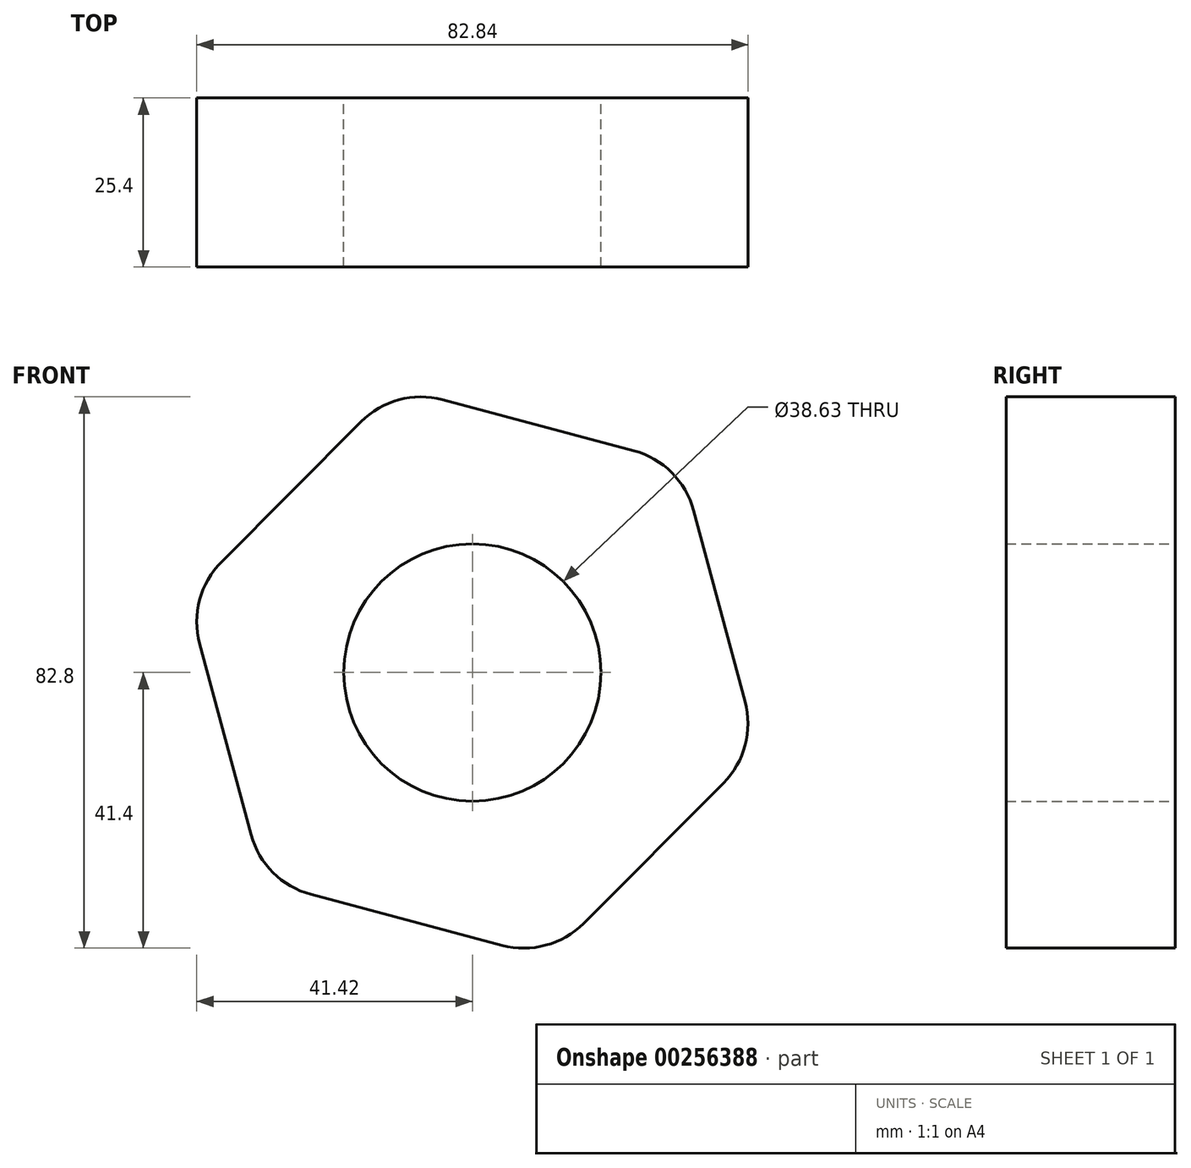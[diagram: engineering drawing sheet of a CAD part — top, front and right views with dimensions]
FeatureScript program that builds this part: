
annotation { "Feature Type Name" : "Feature", "Feature Type Description" : "" }
export const myFeature = defineFeature(function(context is Context, id is Id, definition is map)
    precondition{}
    {
        {
            var Q0;
            Q0=qCreatedBy(makeId("Front.planeOp"),FACE);
            var sketch = newSketch(context, id + "F0", { "sketchPlane" : qUnion([Q0])});
            skCircle(sketch, "E0.cCircle", {"center": v(0, 0) * mm, "radius": 44.39 * mm, "construction": true});
            skLineSegment(sketch, "E0.0", {"start": v(31.34, 31.44) * mm, "end": v(42.9, -11.42) * mm});
            skLineSegment(sketch, "E0.1", {"start": v(42.9, -11.42) * mm, "end": v(11.56, -42.86) * mm});
            skLineSegment(sketch, "E0.2", {"start": v(11.56, -42.86) * mm, "end": v(-31.34, -31.44) * mm});
            skLineSegment(sketch, "E0.3", {"start": v(-31.34, -31.44) * mm, "end": v(-42.9, 11.42) * mm});
            skLineSegment(sketch, "E0.4", {"start": v(-42.9, 11.42) * mm, "end": v(-11.56, 42.86) * mm});
            skLineSegment(sketch, "E0.5", {"start": v(-11.56, 42.86) * mm, "end": v(31.34, 31.44) * mm});
            skCircle(sketch, "E1", {"center": v(0, 0) * mm, "radius": 19.32 * mm});
            skSolve(sketch);
        }
        {
            var Q0;
            Q0 = qSketchRegion(id + "F0", true);
            extrude(context, id + "F1", {"entities" : qUnion([Q0]), "depth" : 25.4 * mm});
        }
        {
            var Q0;
            Q0=makeQuery(id+"F1.opExtrude","SWEPT_EDGE",EDGE,{"disambiguationData":[OSD([sQuery(id+"F0.wireOp",EDGE,"E0.3"),sQuery(id+"F0.wireOp",EDGE,"E0.4")])]});
            var Q1;
            Q1=makeQuery(id+"F1.opExtrude","SWEPT_EDGE",EDGE,{"disambiguationData":[OSD([sQuery(id+"F0.wireOp",EDGE,"E0.2"),sQuery(id+"F0.wireOp",EDGE,"E0.3")])]});
            var Q2;
            Q2=makeQuery(id+"F1.opExtrude","SWEPT_EDGE",EDGE,{"disambiguationData":[OSD([sQuery(id+"F0.wireOp",EDGE,"E0.1"),sQuery(id+"F0.wireOp",EDGE,"E0.2")])]});
            var Q3;
            Q3=makeQuery(id+"F1.opExtrude","SWEPT_EDGE",EDGE,{"disambiguationData":[OSD([sQuery(id+"F0.wireOp",EDGE,"E0.0"),sQuery(id+"F0.wireOp",EDGE,"E0.1")])]});
            var Q4;
            Q4=makeQuery(id+"F1.opExtrude","SWEPT_EDGE",EDGE,{"disambiguationData":[OSD([sQuery(id+"F0.wireOp",EDGE,"E0.0"),sQuery(id+"F0.wireOp",EDGE,"E0.5")])]});
            var Q5;
            Q5=makeQuery(id+"F1.opExtrude","SWEPT_EDGE",EDGE,{"disambiguationData":[OSD([sQuery(id+"F0.wireOp",EDGE,"E0.4"),sQuery(id+"F0.wireOp",EDGE,"E0.5")])]});
            fillet(context, id + "F2", {"entities" : qUnion([Q0, Q1, Q2, Q3, Q4, Q5]), "radius" : 12.7 * mm, "tangentPropagation" : true, "allowEdgeOverflow" : false});
        }
    });
